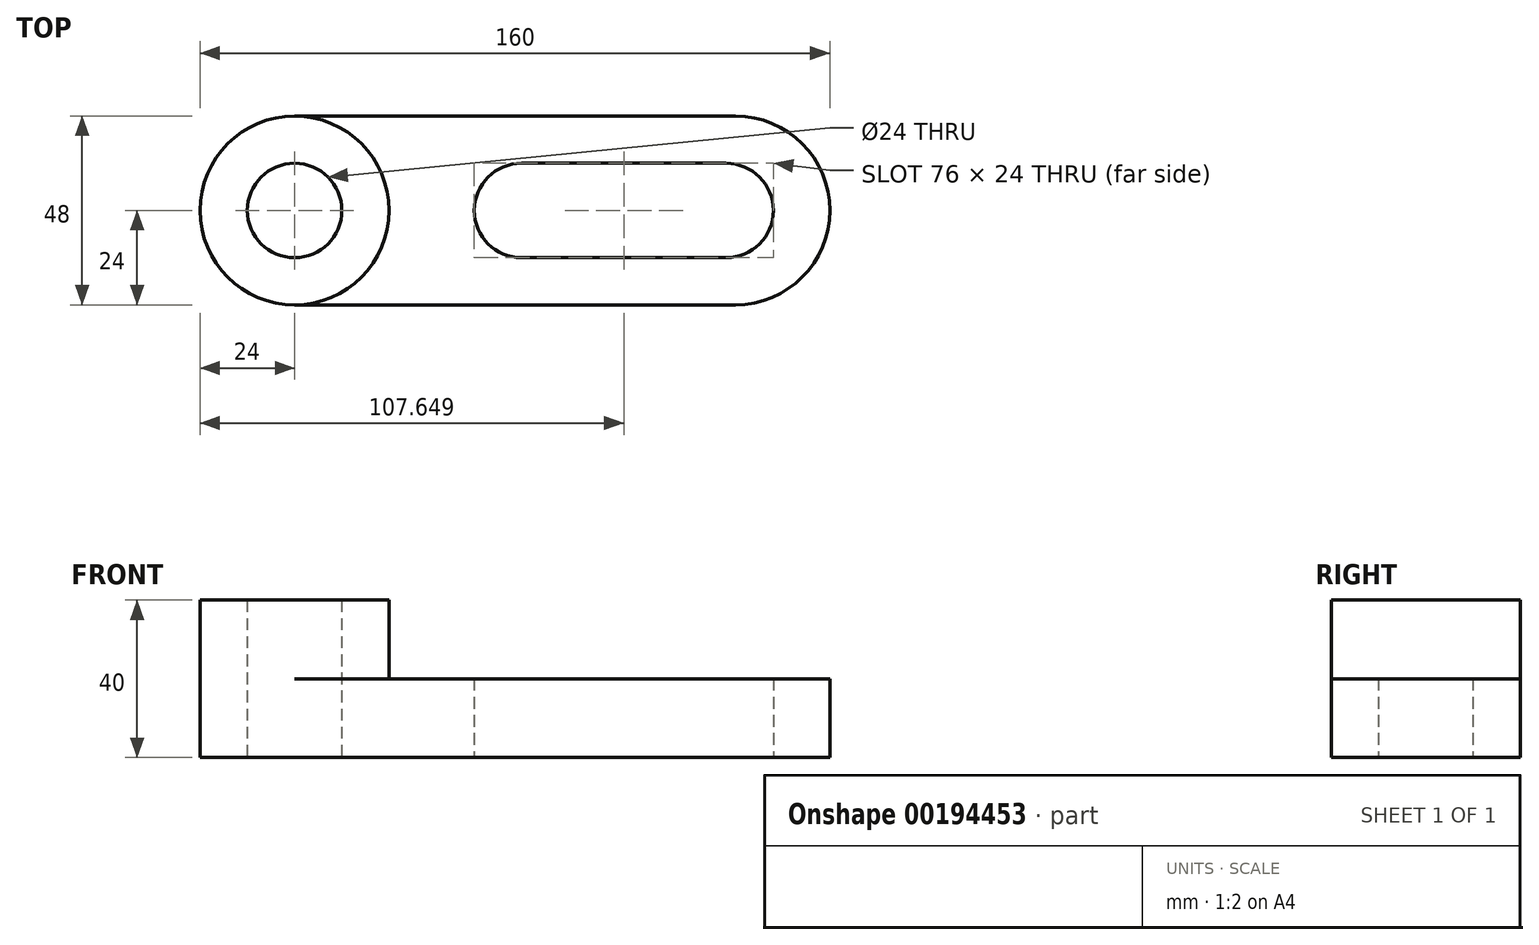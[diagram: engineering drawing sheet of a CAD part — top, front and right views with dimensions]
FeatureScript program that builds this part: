
annotation { "Feature Type Name" : "Feature", "Feature Type Description" : "" }
export const myFeature = defineFeature(function(context is Context, id is Id, definition is map)
    precondition{}
    {
        {
            var Q0;
            Q0=qCreatedBy(makeId("Top.planeOp"),FACE);
            var sketch = newSketch(context, id + "F0", { "sketchPlane" : qUnion([Q0])});
            skArc(sketch, "E0", {"start": v(0, 24) * mm, "mid": v(-24, 0) * mm, "end": v(0, -24) * mm});
            skArc(sketch, "E1", {"start": v(112, -24) * mm, "mid": v(136, 0) * mm, "end": v(112, 24) * mm});
            skLineSegment(sketch, "E2", {"start": v(0, -24) * mm, "end": v(112, -24) * mm});
            skLineSegment(sketch, "E3", {"start": v(112, 24) * mm, "end": v(0, 24) * mm});
            skSolve(sketch);
        }
        {
            var Q0;
            Q0 = qSketchRegion(id + "F0", true);
            extrude(context, id + "F1", {"entities" : qUnion([Q0]), "depth" : 20 * mm});
        }
        {
            var Q0;
            Q0=qCreatedBy(makeId("Top.planeOp"),FACE);
            var sketch = newSketch(context, id + "F2", { "sketchPlane" : qUnion([Q0])});
            skCircle(sketch, "E4", {"center": v(0, 0) * mm, "radius": 24 * mm});
            skSolve(sketch);
        }
        {
            var Q0;
            Q0 = qSketchRegion(id + "F2", true);
            extrude(context, id + "F3", {"entities" : qUnion([Q0]), "operationType" : NewBodyOperationType.ADD, "depth" : 40 * mm});
        }
        {
            var Q0;
            Q0=qCreatedBy(makeId("Top.planeOp"),FACE);
            var sketch = newSketch(context, id + "F4", { "sketchPlane" : qUnion([Q0])});
            skCircle(sketch, "E5", {"center": v(0, 0) * mm, "radius": 12 * mm});
            skArc(sketch, "E6", {"start": v(57.65, 12) * mm, "mid": v(45.65, 0) * mm, "end": v(57.65, -12) * mm});
            skArc(sketch, "E7", {"start": v(109.65, -12) * mm, "mid": v(121.65, 0) * mm, "end": v(109.65, 12) * mm});
            skLineSegment(sketch, "E8", {"start": v(57.65, -12) * mm, "end": v(109.65, -12) * mm});
            skLineSegment(sketch, "E9", {"start": v(109.65, 12) * mm, "end": v(57.65, 12) * mm});
            skSolve(sketch);
        }
        {
            var Q0;
            Q0 = qSketchRegion(id + "F4", true);
            extrude(context, id + "F5", {"entities" : qUnion([Q0]), "operationType" : NewBodyOperationType.REMOVE, "endBound" : BoundingType.THROUGH_ALL, "depth" : 25 * mm});
        }
    });
